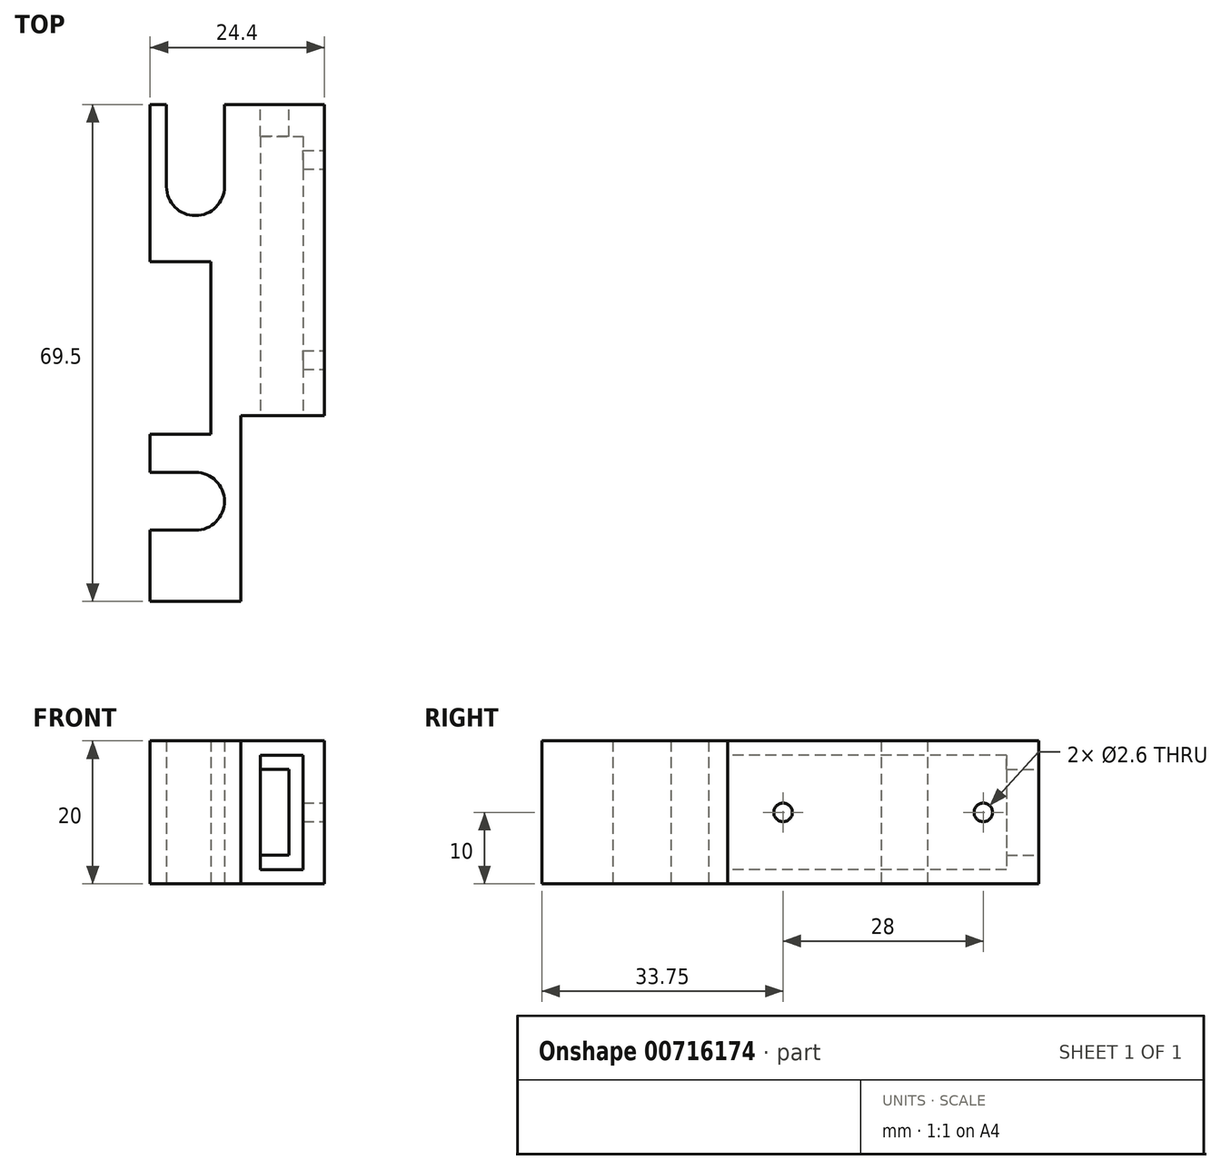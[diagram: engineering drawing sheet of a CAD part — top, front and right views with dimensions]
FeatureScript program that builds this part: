
annotation { "Feature Type Name" : "Feature", "Feature Type Description" : "" }
export const myFeature = defineFeature(function(context is Context, id is Id, definition is map)
    precondition{}
    {
        {
            var Q0;
            Q0=qCreatedBy(makeId("Top.planeOp"),FACE);
            var sketch = newSketch(context, id + "F0", { "sketchPlane" : qUnion([Q0])});
            skArc(sketch, "E0", {"start": v(0, -4.05) * mm, "mid": v(4.05, 0) * mm, "end": v(0, 4.05) * mm});
            skArc(sketch, "E1", {"start": v(-4.05, 44) * mm, "mid": v(0, 39.95) * mm, "end": v(4.05, 44) * mm});
            skLineSegment(sketch, "E2.bottom", {"start": v(6.35, 55.5) * mm, "end": v(4.05, 55.5) * mm});
            skLineSegment(sketch, "E2.right", {"start": v(-6.35, 55.5) * mm, "end": v(-6.35, 33.5) * mm});
            skLineSegment(sketch, "E3", {"start": v(6.35, 55.5) * mm, "end": v(18.05, 55.5) * mm});
            skLineSegment(sketch, "E4", {"start": v(18.05, 55.5) * mm, "end": v(18.05, 12) * mm});
            skLineSegment(sketch, "E5", {"start": v(18.05, 12) * mm, "end": v(6.35, 12) * mm});
            skLineSegment(sketch, "E6", {"start": v(6.35, 12) * mm, "end": v(6.35, -14) * mm});
            skLineSegment(sketch, "E7", {"start": v(6.35, -14) * mm, "end": v(-6.35, -14) * mm});
            skLineSegment(sketch, "E8", {"start": v(-6.35, -14) * mm, "end": v(-6.35, -4.05) * mm});
            skLineSegment(sketch, "E9", {"start": v(0, -4.05) * mm, "end": v(-6.35, -4.05) * mm});
            skLineSegment(sketch, "E10", {"start": v(0, 4.05) * mm, "end": v(-6.35, 4.05) * mm});
            skLineSegment(sketch, "E11", {"start": v(-6.35, 4.05) * mm, "end": v(-6.35, 9.35) * mm});
            skLineSegment(sketch, "E12", {"start": v(-6.35, 9.35) * mm, "end": v(2.15, 9.35) * mm});
            skLineSegment(sketch, "E13", {"start": v(2.15, 9.35) * mm, "end": v(2.15, 32.5) * mm});
            skLineSegment(sketch, "E14", {"start": v(-6.35, 33.5) * mm, "end": v(2.15, 33.5) * mm});
            skLineSegment(sketch, "E15", {"start": v(2.15, 33.5) * mm, "end": v(2.15, 32.5) * mm});
            skPoint(sketch, "E16.orphan", {"position": v(-6.35, 32.5) * mm});
            skLineSegment(sketch, "E17", {"start": v(-4.05, 44) * mm, "end": v(-4.05, 55.5) * mm});
            skLineSegment(sketch, "E18", {"start": v(4.05, 44) * mm, "end": v(4.05, 55.5) * mm});
            skLineSegment(sketch, "E19.trimOffspring", {"start": v(-4.05, 55.5) * mm, "end": v(-6.35, 55.5) * mm});
            skPoint(sketch, "E20.start.orphan", {"position": v(0, 39.95) * mm});
            skSolve(sketch);
        }
        {
            var Q0;
            Q0=makeQuery(id+"F0.imprint","IMPRINT",FACE,{"disambiguationData":[TD([[makeQuery(id+"F0.imprint","IMPRINT",EDGE,{"derivedFrom":sQuery(id+"F0.wireOp",EDGE,"E0")}),-1.0]])]});
            extrude(context, id + "F1", {"entities" : qUnion([Q0]), "depth" : 20 * mm, "offsetDistance" : 25 * mm});
        }
        {
            var Q0;
            Q0=makeQuery(id+"F1.opExtrude","SWEPT_FACE",FACE,{"disambiguationData":[OSD([sQuery(id+"F0.wireOp",EDGE,"E2.bottom"),sQuery(id+"F0.wireOp",EDGE,"E3")])]});
            var sketch = newSketch(context, id + "F2", { "sketchPlane" : qUnion([Q0])});
            skLineSegment(sketch, "E21.0.0", {"start": v(-18.05, 0) * mm, "end": v(-4.05, 0) * mm});
            skLineSegment(sketch, "E21.0.1", {"start": v(-4.05, 0) * mm, "end": v(-4.05, 20) * mm});
            skLineSegment(sketch, "E21.0.2", {"start": v(-4.05, 20) * mm, "end": v(-18.05, 20) * mm});
            skLineSegment(sketch, "E21.0.3", {"start": v(-18.05, 20) * mm, "end": v(-18.05, 0) * mm});
            skLineSegment(sketch, "E22.bottom", {"start": v(-9.05, 4) * mm, "end": v(-13.05, 4) * mm});
            skLineSegment(sketch, "E22.top", {"start": v(-9.05, 16) * mm, "end": v(-13.05, 16) * mm});
            skLineSegment(sketch, "E22.left", {"start": v(-9.05, 4) * mm, "end": v(-9.05, 16) * mm});
            skLineSegment(sketch, "E22.right", {"start": v(-13.05, 4) * mm, "end": v(-13.05, 16) * mm});
            skPoint(sketch, "E22.middle", {"position": v(-11.05, 10) * mm});
            skPoint(sketch, "E22.middle.positionSnap0", {"position": v(-4.05, 10) * mm});
            skPoint(sketch, "E22.middle.positionSnap1", {"position": v(-11.05, 0) * mm});
            skPoint(sketch, "E22.centerSnap0", {"position": v(-4.05, 10) * mm});
            skPoint(sketch, "E22.centerSnap1", {"position": v(-11.05, 0) * mm});
            skSolve(sketch);
        }
        {
            var Q0;
            Q0=makeQuery(id+"F2.imprint","IMPRINT",FACE,{"disambiguationData":[TD([[makeQuery(id+"F2.imprint","IMPRINT",EDGE,{"derivedFrom":sQuery(id+"F2.wireOp",EDGE,"E22.bottom")}),-1.0]])]});
            extrude(context, id + "F3", {"entities" : qUnion([Q0]), "operationType" : NewBodyOperationType.REMOVE, "oppositeDirection" : true, "depth" : 59 * mm, "offsetDistance" : 25 * mm});
        }
        {
            var Q0;
            Q0=makeQuery(id+"F1.opExtrude","SWEPT_FACE",FACE,{"disambiguationData":[OSD([sQuery(id+"F0.wireOp",EDGE,"E5")])]});
            var sketch = newSketch(context, id + "F4", { "sketchPlane" : qUnion([Q0])});
            skLineSegment(sketch, "E23.bottom", {"start": v(9.05, 16) * mm, "end": v(15.05, 16) * mm});
            skLineSegment(sketch, "E23.top", {"start": v(9.05, 4) * mm, "end": v(15.05, 4) * mm});
            skLineSegment(sketch, "E23.left", {"start": v(9.05, 16) * mm, "end": v(9.05, 4) * mm});
            skLineSegment(sketch, "E23.right", {"start": v(15.05, 16) * mm, "end": v(15.05, 4) * mm});
            skLineSegment(sketch, "E24", {"start": v(9.05, 10) * mm, "end": v(9.05, 2) * mm});
            skLineSegment(sketch, "E25", {"start": v(9.05, 2) * mm, "end": v(15.05, 2) * mm});
            skLineSegment(sketch, "E26", {"start": v(15.05, 2) * mm, "end": v(15.05, 4) * mm});
            skLineSegment(sketch, "E27", {"start": v(9.05, 10) * mm, "end": v(9.05, 18) * mm});
            skLineSegment(sketch, "E28", {"start": v(9.05, 18) * mm, "end": v(15.05, 18) * mm});
            skLineSegment(sketch, "E29", {"start": v(15.05, 18) * mm, "end": v(15.05, 16) * mm});
            skSolve(sketch);
        }
        {
            var Q0;
            {var subQ2=sQuery(id+"F4.wireOp",EDGE,"E23.right");Q0=makeQuery(id+"F4.imprint","IMPRINT",FACE,{"disambiguationData":[TD([[makeQuery(id+"F4.imprint","IMPRINT",EDGE,{"derivedFrom":subQ2}),-1.0]])]});}
            var Q1;
            {var subQ3=sQuery(id+"F4.wireOp",EDGE,"E25");Q1=makeQuery(id+"F4.imprint","IMPRINT",FACE,{"disambiguationData":[TD([[makeQuery(id+"F4.imprint","IMPRINT",EDGE,{"derivedFrom":subQ3}),1.0]])]});}
            var Q2;
            {var subQ3=sQuery(id+"F4.wireOp",EDGE,"E28");Q2=makeQuery(id+"F4.imprint","IMPRINT",FACE,{"disambiguationData":[TD([[makeQuery(id+"F4.imprint","IMPRINT",EDGE,{"derivedFrom":subQ3}),-1.0]])]});}
            extrude(context, id + "F5", {"entities" : qUnion([Q0, Q1, Q2]), "operationType" : NewBodyOperationType.REMOVE, "oppositeDirection" : true, "depth" : 39 * mm, "offsetDistance" : 25 * mm});
        }
        {
            var Q0;
            Q0=makeQuery(id+"F1.opExtrude","SWEPT_FACE",FACE,{"disambiguationData":[OSD([sQuery(id+"F0.wireOp",EDGE,"E4")])]});
            var sketch = newSketch(context, id + "F6", { "sketchPlane" : qUnion([Q0])});
            skLineSegment(sketch, "E30", {"start": v(12, 10) * mm, "end": v(55.5, 10) * mm, "construction": true});
            skLineSegment(sketch, "E31", {"start": v(33.75, 20) * mm, "end": v(33.75, 0) * mm, "construction": true});
            skCircle(sketch, "E32", {"center": v(19.75, 10) * mm, "radius": 1.3 * mm});
            skCircle(sketch, "E33", {"center": v(47.75, 10) * mm, "radius": 1.3 * mm});
            skSolve(sketch);
        }
        {
            var Q0;
            Q0=makeQuery(id+"F6.imprint","IMPRINT",FACE,{"disambiguationData":[TD([[makeQuery(id+"F6.imprint","IMPRINT",EDGE,{"derivedFrom":sQuery(id+"F6.wireOp",EDGE,"E33")}),1.0]])]});
            var Q1;
            Q1=makeQuery(id+"F6.imprint","IMPRINT",FACE,{"disambiguationData":[TD([[makeQuery(id+"F6.imprint","IMPRINT",EDGE,{"derivedFrom":sQuery(id+"F6.wireOp",EDGE,"E32")}),1.0]])]});
            extrude(context, id + "F7", {"entities" : qUnion([Q0, Q1]), "operationType" : NewBodyOperationType.REMOVE, "oppositeDirection" : true, "depth" : 7.3 * mm, "offsetDistance" : 25 * mm});
        }
    });
